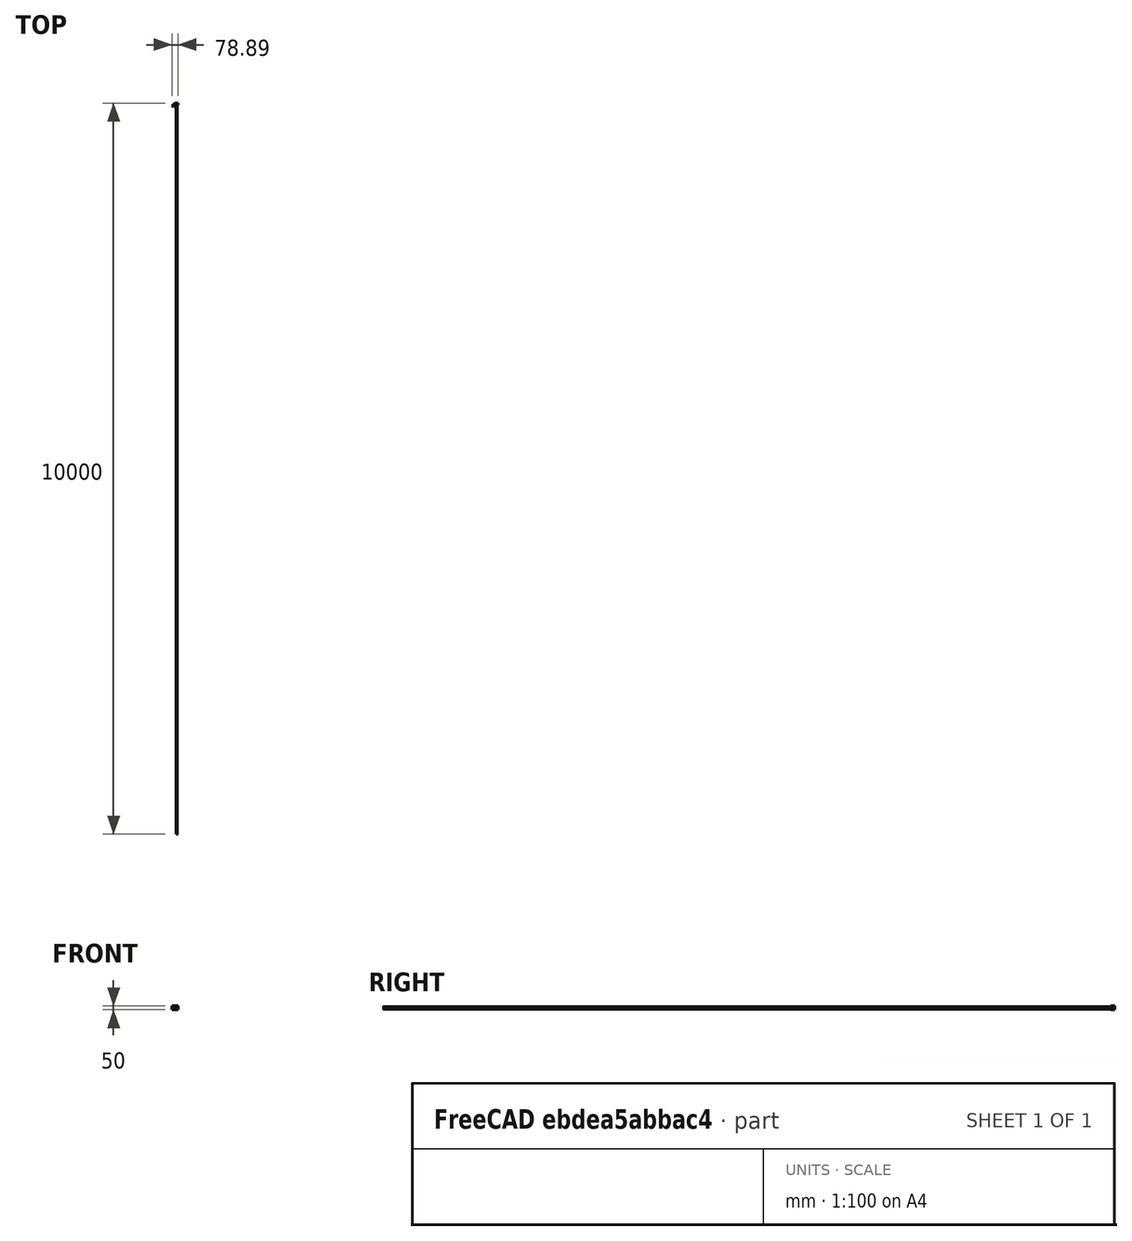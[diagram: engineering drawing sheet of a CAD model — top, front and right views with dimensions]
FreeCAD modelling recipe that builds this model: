
FCSTD DOCUMENT  (FreeCAD 0.16R)
Label: chuckKey
License: All rights reserved
LicenseURL: http://en.wikipedia.org/wiki/All_rights_reserved
objects: Sketcher::SketchObject×3, PartDesign::Pocket×2, PartDesign::Chamfer×2, PartDesign::Pad×1, PartDesign::Fillet×1, Mesh::Feature×1
note: 12 computed .brp shape members not serialized (recipe doc carries the construction recipe); baked Part::Feature solids carry a one-line shape summary decoded from their .brp

FEATURE [Sketcher::SketchObject] Sketch
  sketch-geometry (6):
    g0: LineSegment StartX=0 StartY=20 StartZ=0 EndX=-40 EndY=20 EndZ=0
    g1: LineSegment StartX=-40 StartY=20 StartZ=0 EndX=-78.8909 EndY=-18.8909 EndZ=0
    g2: LineSegment StartX=-78.8909 StartY=-18.8909 StartZ=0 EndX=-64.7487 EndY=-33.033 EndZ=0
    g3: LineSegment StartX=-64.7487 StartY=-33.033 StartZ=0 EndX=-31.7157 EndY=0 EndZ=0
    g4: LineSegment StartX=-31.7157 StartY=0 StartZ=0 EndX=0 EndY=0 EndZ=0
    g5: LineSegment StartX=0 StartY=0 StartZ=0 EndX=0 EndY=20 EndZ=0
  constraints (17):
    c: Horizontal(g0)
    c: Coincident(g0,g1)
    c: Coincident(g1,g2)
    c: Coincident(g2,g3)
    c: Coincident(g3,g4)
    c: Coincident(g4,g5)
    c: Coincident(g5,g0)
    c: Vertical(g5)
    c: Horizontal(g4)
    c: Parallel(g3,g1)
    c: Perpendicular(g1,g2)
    c: Distance(g2) = 20
    c: Distance(g5) = 20
    c: Distance(g1) = 55
    c: Distance(g0) = 40
    c: Coincident(g4,g-1)
    c: Angle(g1) = -2.35619
FEATURE [PartDesign::Pad] Pad
  Length = 50
  Length2 = 100
  Sketch = -> Sketch
  Type = 0
FEATURE [Sketcher::SketchObject] Sketch001
  Placement = pos=(-30,30,0) rot=(-0.281085,0.678598,0.678598;3.68962rad)
  Support = -> Pad [Face2]
  sketch-geometry (2):
    g0: Circle CenterX=29.8344 CenterY=33.566 CenterZ=0 NormalX=0 NormalY=0 NormalZ=1 Radius=11
    g1: Circle CenterX=52.3286 CenterY=15.325 CenterZ=0 NormalX=0 NormalY=0 NormalZ=1 Radius=11
  constraints (2):
    c: Radius(g1) = 11
    c: Equal(g1,g0)
FEATURE [PartDesign::Pocket] Pocket
  Length = 5
  Sketch = -> Sketch001
  Type = 1
FEATURE [PartDesign::Fillet] Fillet
  Base = -> Pocket [Edge13,Edge16]
  Radius = 7
FEATURE [PartDesign::Chamfer] Chamfer
  Base = -> Fillet [Edge1,Edge2,Edge3,Edge4,Edge5,Edge6,Edge7,Edge8,Edge16,Edge10,Edge17]
  Size = 1.5
FEATURE [PartDesign::Chamfer] Chamfer001
  Base = -> Chamfer [Edge58]
  Size = 3
FEATURE [Sketcher::SketchObject] Sketch002
  Placement = pos=(0,20,0) rot=(0,0.707107,0.707107;3.14159rad)
  Support = -> Chamfer001 [Face17]
  sketch-geometry (2):
    g0: Circle CenterX=22.6945 CenterY=37.2126 CenterZ=0 NormalX=0 NormalY=0 NormalZ=1 Radius=3
    g1: Circle CenterX=12.8616 CenterY=11.9317 CenterZ=0 NormalX=0 NormalY=0 NormalZ=1 Radius=3
  constraints (2):
    c: Radius(g1) = 3
    c: Equal(g1,g0)
FEATURE [PartDesign::Pocket] Pocket001
  Length = 5
  Sketch = -> Sketch002
  Type = 1
FEATURE [Mesh::Feature] Mesh  label="Pocket001 (Meshed)"
